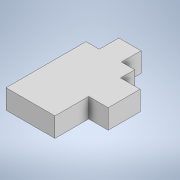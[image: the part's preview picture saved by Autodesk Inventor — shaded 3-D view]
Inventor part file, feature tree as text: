
AUTODESK INVENTOR PART (.ipt)
format: ipt  version: 2020 (Build 240168000, 168)  size: 108,544 bytes
history: native  units: mm
features: extrude x1, sketch x1
ambient origin geometry x8: Origin, YZ Plane, XZ Plane, XY Plane, X Axis, Y Axis, Z Axis, Center Point
bodies: Solide1 (feature_tree)
feature tree (2):
  extrude  "Extrusion1"  Depth=90.0mm
  sketch  "Esquisse1"
